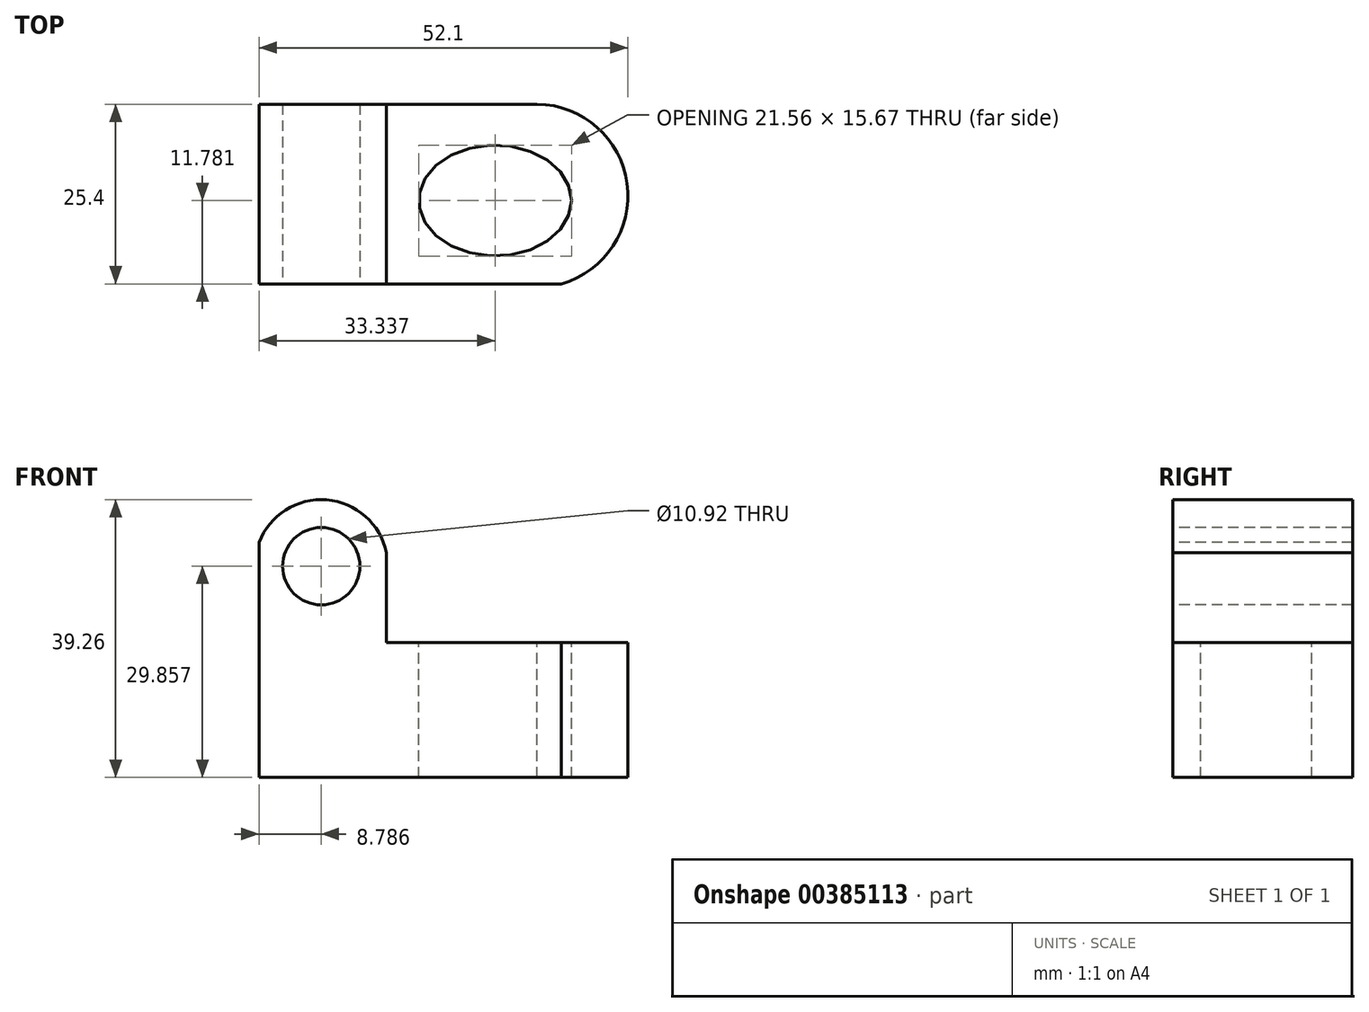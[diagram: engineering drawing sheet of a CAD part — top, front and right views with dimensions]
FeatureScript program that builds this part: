
annotation { "Feature Type Name" : "Feature", "Feature Type Description" : "" }
export const myFeature = defineFeature(function(context is Context, id is Id, definition is map)
    precondition{}
    {
        {
            var Q0;
            Q0=qCreatedBy(makeId("Front.planeOp"),FACE);
            var sketch = newSketch(context, id + "F0", { "sketchPlane" : qUnion([Q0])});
            skLineSegment(sketch, "E0", {"start": v(0, 0) * mm, "end": v(0, 44.45) * mm});
            skLineSegment(sketch, "E1", {"start": v(0, 44.45) * mm, "end": v(18, 44.45) * mm});
            skLineSegment(sketch, "E2", {"start": v(18, 44.45) * mm, "end": v(18, 19.05) * mm});
            skLineSegment(sketch, "E3", {"start": v(18, 19.05) * mm, "end": v(53.67, 19.05) * mm});
            skLineSegment(sketch, "E4", {"start": v(53.67, 19.05) * mm, "end": v(53.67, 0) * mm});
            skLineSegment(sketch, "E5", {"start": v(53.67, 0) * mm, "end": v(0, 0) * mm});
            skSolve(sketch);
        }
        {
            var Q0;
            Q0 = qSketchRegion(id + "F0", true);
            extrude(context, id + "F1", {"entities" : qUnion([Q0]), "depth" : 25.4 * mm});
        }
        {
            var Q0;
            Q0=makeQuery(id+"F1.opExtrude","CAP_FACE",FACE,{"disambiguationData":[OSD([sQuery(id+"F0.wireOp",EDGE,"E0"),sQuery(id+"F0.wireOp",EDGE,"E1"),sQuery(id+"F0.wireOp",EDGE,"E2"),sQuery(id+"F0.wireOp",EDGE,"E3"),sQuery(id+"F0.wireOp",EDGE,"E4"),sQuery(id+"F0.wireOp",EDGE,"E5")])],"isStart":false});
            var sketch = newSketch(context, id + "F2", { "sketchPlane" : qUnion([Q0])});
            skArc(sketch, "E6", {"start": v(18, 31.75) * mm, "mid": v(9.54, 39.23) * mm, "end": v(0, 33.2) * mm});
            skSolve(sketch);
        }
        {
            var Q0;
            {var subQ0=sQuery(id+"F2.wireOp",EDGE,"E6");Q0=makeQuery(id+"F2.imprint","IMPRINT",FACE,{"disambiguationData":[TD([[makeQuery(id+"F2.imprint","IMPRINT",EDGE,{"derivedFrom":subQ0}),-1.0]])]});}
            extrude(context, id + "F3", {"entities" : qUnion([Q0]), "operationType" : NewBodyOperationType.REMOVE, "oppositeDirection" : true, "depth" : 25.4 * mm});
        }
        {
            var Q0;
            Q0=makeQuery(id+"F1.opExtrude","SWEPT_FACE",FACE,{"disambiguationData":[OSD([sQuery(id+"F0.wireOp",EDGE,"E3")])]});
            var sketch = newSketch(context, id + "F4", { "sketchPlane" : qUnion([Q0])});
            skArc(sketch, "E7", {"start": v(42.7, -25.4) * mm, "mid": v(51.96, -11.09) * mm, "end": v(39.01, 0) * mm});
            skSolve(sketch);
        }
        {
            var Q0;
            {var subQ1=sQuery(id+"F0.wireOp",EDGE,"E3");var subQ6=makeQuery(id+"F1.opExtrude","SWEPT_EDGE",EDGE,{"disambiguationData":[OSD([subQ1,sQuery(id+"F0.wireOp",EDGE,"E4")])]});Q0=makeQuery(id+"F4.imprint","IMPRINT",FACE,{"disambiguationData":[TD([[makeQuery(id+"F4.imprint","IMPRINT",EDGE,{"derivedFrom":subQ6}),1.0]])]});}
            extrude(context, id + "F5", {"entities" : qUnion([Q0]), "operationType" : NewBodyOperationType.REMOVE, "oppositeDirection" : true, "depth" : 25.4 * mm});
        }
        {
            var Q0;
            Q0=makeQuery(id+"F1.opExtrude","CAP_FACE",FACE,{"disambiguationData":[OSD([sQuery(id+"F0.wireOp",EDGE,"E0"),sQuery(id+"F0.wireOp",EDGE,"E1"),sQuery(id+"F0.wireOp",EDGE,"E2"),sQuery(id+"F0.wireOp",EDGE,"E3"),sQuery(id+"F0.wireOp",EDGE,"E4"),sQuery(id+"F0.wireOp",EDGE,"E5")])],"isStart":false});
            var sketch = newSketch(context, id + "F6", { "sketchPlane" : qUnion([Q0])});
            skCircle(sketch, "E8", {"center": v(8.79, 29.86) * mm, "radius": 5.46 * mm});
            skSolve(sketch);
        }
        {
            var Q0;
            Q0=makeQuery(id+"F6.imprint","IMPRINT",FACE,{"disambiguationData":[TD([[makeQuery(id+"F6.imprint","IMPRINT",EDGE,{"derivedFrom":sQuery(id+"F6.wireOp",EDGE,"E8")}),1.0]])]});
            extrude(context, id + "F7", {"entities" : qUnion([Q0]), "operationType" : NewBodyOperationType.REMOVE, "oppositeDirection" : true, "depth" : 25.4 * mm});
        }
        {
            var Q0;
            Q0=makeQuery(id+"F1.opExtrude","SWEPT_FACE",FACE,{"disambiguationData":[OSD([sQuery(id+"F0.wireOp",EDGE,"E3")])]});
            var sketch = newSketch(context, id + "F8", { "sketchPlane" : qUnion([Q0])});
            skEllipse(sketch, "E9", {"center": v(33.34, -13.62) * mm, "majorRadius": 10.78 * mm, "minorRadius": 7.84 * mm, "majorAxis": v(1, 0)});
            skSolve(sketch);
        }
        {
            var Q0;
            Q0=makeQuery(id+"F8.imprint","IMPRINT",FACE,{"disambiguationData":[TD([[makeQuery(id+"F8.imprint","IMPRINT",EDGE,{"derivedFrom":sQuery(id+"F8.wireOp",EDGE,"E9")}),1.0]])]});
            extrude(context, id + "F9", {"entities" : qUnion([Q0]), "operationType" : NewBodyOperationType.REMOVE, "oppositeDirection" : true, "depth" : 25.4 * mm});
        }
    });
